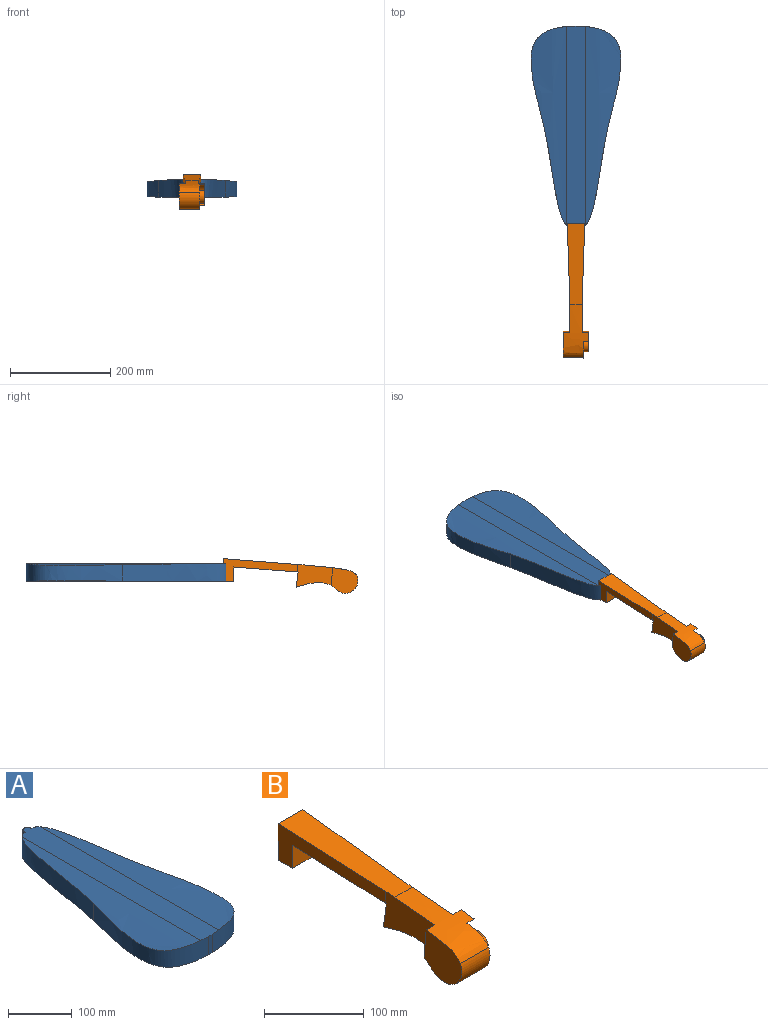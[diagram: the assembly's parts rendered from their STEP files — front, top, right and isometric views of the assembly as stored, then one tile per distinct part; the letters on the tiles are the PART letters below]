
ASSEMBLY  parts=2 mates=1
PART A: 20 faces, bbox 179.5x412x35 mm
  f0: plane 412x40.13mm, normal (0,0,1), area 16133.4mm2, adj f2,f3,f4,f5,f6,f7,f11,f12
  f1: plane 412x37.61mm, normal (0,0,-1), area 15159.8mm2, adj f2,f3,f4,f5,f6,f7,f9,f12
  f2: plane 35x5mm, normal (0,1,0), area 175mm2, adj f0,f1,f3,f7
  f3: plane 35x2mm, normal (1,0,0), area 70mm2, adj f0,f1,f2,f4
  f4: cylinder r=7.5mm len=35mm, axis (0,0,-1), area 824.7mm2, adj f0,f1,f3,f13
  f5: plane 35x8mm, normal (0,-1,0), area 280mm2, adj f0,f1,f6,f14
  f6: extruded ~192.42x85.74mm, area 8033.5mm2, adj f0,f1,f5,f7,f8,f9,f10,f11
  f7: extruded ~210.08x53.4mm, area 7563.6mm2, adj f0,f1,f2,f6,f8,f9,f10,f11
  f8: plane 394.81x47.15mm, normal (0,0,-1), area 12027.5mm2, adj f6,f7,f9,f10
  f9: extruded ~397.18x5.63mm, area 2211.4mm2, adj f1,f6,f7,f8
  f10: extruded ~183.95x25.2mm, area 2980.9mm2, adj f6,f7,f8
  f11: extruded ~395.71x69.8mm, area 16757.5mm2, adj f0,f6,f7
  f12: plane 35x5mm, normal (0,1,0), area 175mm2, adj f0,f1,f13,f15
  f13: plane 35x2mm, normal (-1,0,0), area 70mm2, adj f0,f1,f4,f12
  f14: extruded ~192.42x85.74mm, area 8033.5mm2, adj f0,f1,f5,f15,f16,f17,f18,f19
  f15: extruded ~210.08x53.4mm, area 7563.6mm2, adj f0,f1,f12,f14,f16,f17,f18,f19
  f16: plane 394.81x47.15mm, normal (0,0,-1), area 12027.5mm2, adj f14,f15,f17,f18
  f17: extruded ~397.18x5.63mm, area 2211.4mm2, adj f1,f14,f15,f16
  f18: extruded ~183.95x25.2mm, area 2980.9mm2, adj f14,f15,f16
  f19: extruded ~395.71x69.8mm, area 16757.5mm2, adj f0,f14,f15
PART B: 21 faces, bbox 50x268.2x69.2 mm
  f0: cylinder r=25mm len=43.46mm, axis (-1,0,0), area 2786.3mm2, adj f1,f2,f8,f17
  f1: extruded ~105.87x50mm, area 3750.8mm2, adj f0,f8,f9,f10,f11,f12,f14,f15
  f2: extruded ~80.14x50mm, area 2427.7mm2, adj f0,f3,f8,f10,f11,f12,f14,f15
  f3: plane 30x25mm, normal (0,0.99,0.13), area 756.6mm2, adj f2,f4,f11,f14
  f4: plane 128.6x33.57mm, normal (0,0.08,-1), area 3770.8mm2, adj f3,f5,f11,f13,f14,f16
  f5: plane 33.57x28.38mm, normal (0,-1,0), area 950.6mm2, adj f4,f6,f13,f16
  f6: plane 34.76x20mm, normal (0,0,-1), area 681.8mm2, adj f5,f7,f13,f16
  f7: plane 45x35mm, normal (0,1,0), area 1569.7mm2, adj f6,f9,f13,f16
  f8: plane 55.67x55.06mm, normal (-1,0,0), area 2118.2mm2, adj f0,f1,f2,f12
  f9: plane 160.5x35mm, normal (0,-0.08,1), area 4768.1mm2, adj f1,f7,f11,f13,f14,f16
  f10: plane 43.28x21.03mm, normal (1,0,0), area 225.1mm2, adj f1,f2,f15,f18
  f11: plane 73.69x47.06mm, normal (-1,0,0), area 2493.6mm2, adj f1,f2,f3,f4,f9,f12,f13
  f12: plane 35.7x12.5mm, normal (0,1,0.08), area 447.6mm2, adj f1,f2,f8,f11
  f13: plane 148.15x45mm, normal (-1,-0.03,0), area 2805.2mm2, adj f4,f5,f6,f7,f9,f11
  f14: plane 73.69x47.06mm, normal (1,0,0), area 2493.6mm2, adj f1,f2,f3,f4,f9,f15,f16
  f15: plane 35.7x12.5mm, normal (0,1,0.08), area 447.6mm2, adj f1,f2,f10,f14
  f16: plane 148.15x45mm, normal (1,-0.03,0), area 2805.2mm2, adj f4,f5,f6,f7,f9,f14
  f17: plane 51.27x50mm, normal (1,0,0), area 1402.2mm2, adj f0,f1,f18,f19
  f18: cylinder r=25mm len=40.66mm, axis (1,0,0), area 499.9mm2, adj f1,f2,f10,f17
  f19: cylinder r=12.5mm len=25mm, axis (1,0,0), area 785.4mm2, adj f17,f20
  f20: plane 25x25mm, normal (1,0,0), area 490.9mm2, adj f19
PLACE A rot(axis=(0,0,1),180deg) t=(187.66,857.84,500.51)mm
PLACE B t=(187.66,573.05,500.51)mm
MATE fastened A.f4 <-> B.f6  axis (0,0,-1) through (187.66,573.11,500.51)mm
